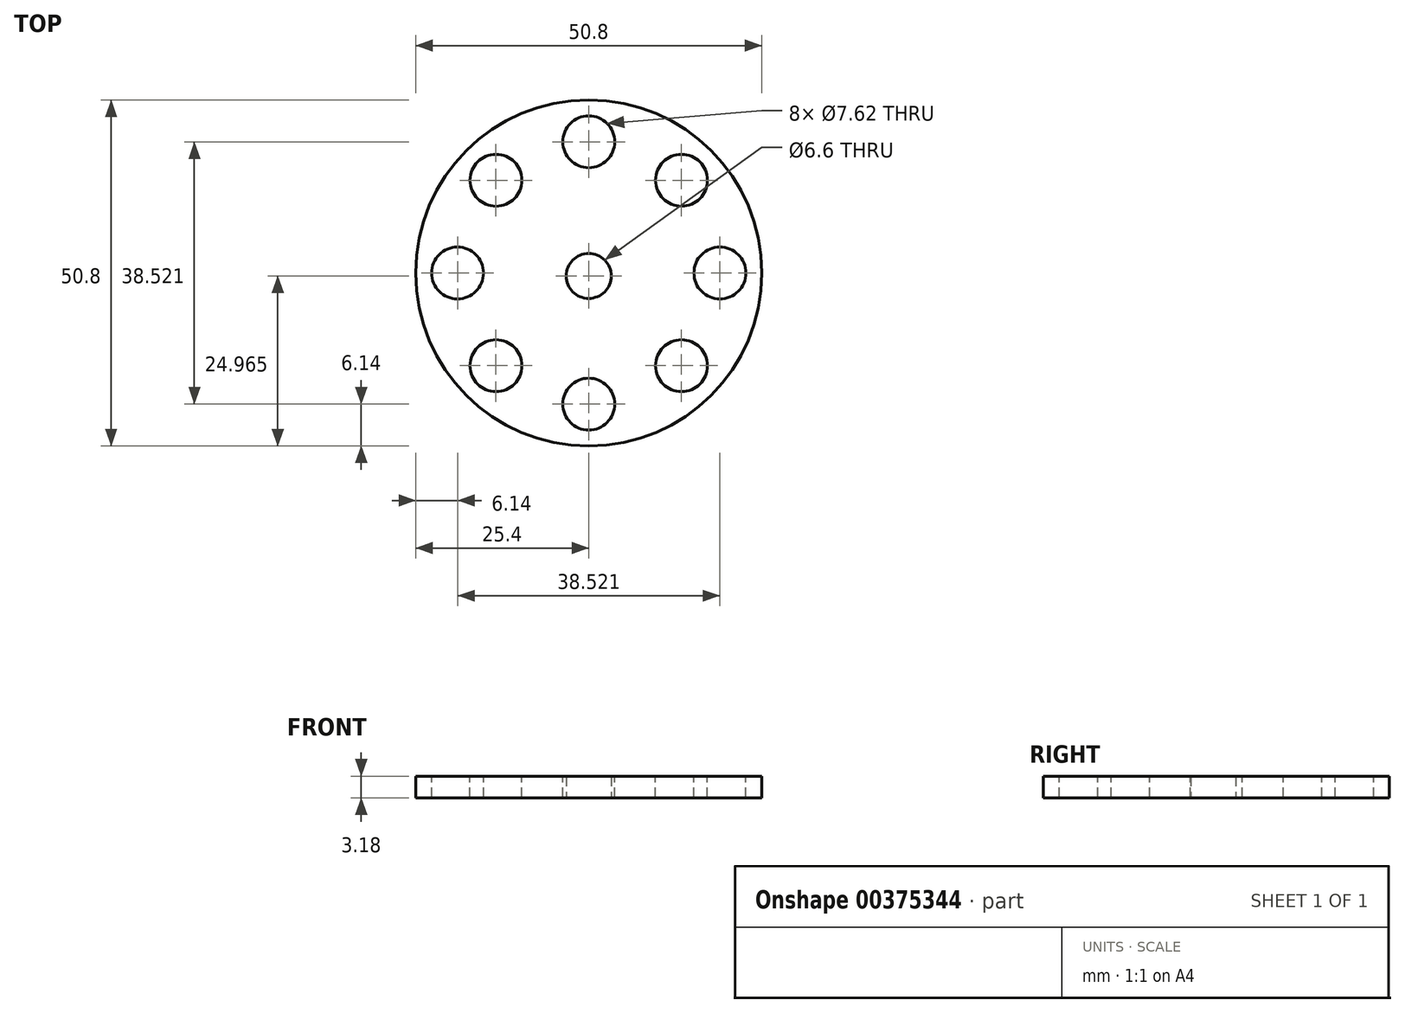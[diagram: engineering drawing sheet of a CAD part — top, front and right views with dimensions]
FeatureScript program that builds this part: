
annotation { "Feature Type Name" : "Feature", "Feature Type Description" : "" }
export const myFeature = defineFeature(function(context is Context, id is Id, definition is map)
    precondition{}
    {
        {
            var Q0;
            Q0=qCreatedBy(makeId("Top.planeOp"),FACE);
            var sketch = newSketch(context, id + "F0", { "sketchPlane" : qUnion([Q0])});
            skCircle(sketch, "E0", {"center": v(0, 0) * mm, "radius": 25.4 * mm});
            skCircle(sketch, "E1", {"center": v(0, -0.44) * mm, "radius": 3.3 * mm});
            skSolve(sketch);
        }
        {
            var Q0;
            Q0 = qSketchRegion(id + "F0", true);
            extrude(context, id + "F1", {"entities" : qUnion([Q0]), "depth" : 3.17 * mm});
        }
        {
            var Q0;
            Q0=makeQuery(id+"F1.opExtrude","CAP_FACE",FACE,{"disambiguationData":[OSD([sQuery(id+"F0.wireOp",EDGE,"E0"),sQuery(id+"F0.wireOp",EDGE,"E1")])],"isStart":false});
            var sketch = newSketch(context, id + "F2", { "sketchPlane" : qUnion([Q0])});
            skCircle(sketch, "E2", {"center": v(0, 19.26) * mm, "radius": 3.81 * mm});
            skCircle(sketch, "E3.1.0", {"center": v(-13.62, 13.62) * mm, "radius": 3.81 * mm});
            skCircle(sketch, "E3.2.0", {"center": v(-19.26, 0) * mm, "radius": 3.81 * mm});
            skCircle(sketch, "E3.3.0", {"center": v(-13.62, -13.62) * mm, "radius": 3.81 * mm});
            skCircle(sketch, "E3.4.0", {"center": v(0, -19.26) * mm, "radius": 3.81 * mm});
            skCircle(sketch, "E3.5.0", {"center": v(13.62, -13.62) * mm, "radius": 3.81 * mm});
            skCircle(sketch, "E3.6.0", {"center": v(19.26, 0) * mm, "radius": 3.81 * mm});
            skCircle(sketch, "E3.7.0", {"center": v(13.62, 13.62) * mm, "radius": 3.81 * mm});
            skPoint(sketch, "E3.center", {"position": v(0, 0) * mm});
            skSolve(sketch);
        }
        {
            var Q0;
            Q0 = qSketchRegion(id + "F2", true);
            extrude(context, id + "F3", {"entities" : qUnion([Q0]), "operationType" : NewBodyOperationType.REMOVE, "oppositeDirection" : true, "depth" : 25.4 * mm});
        }
    });
